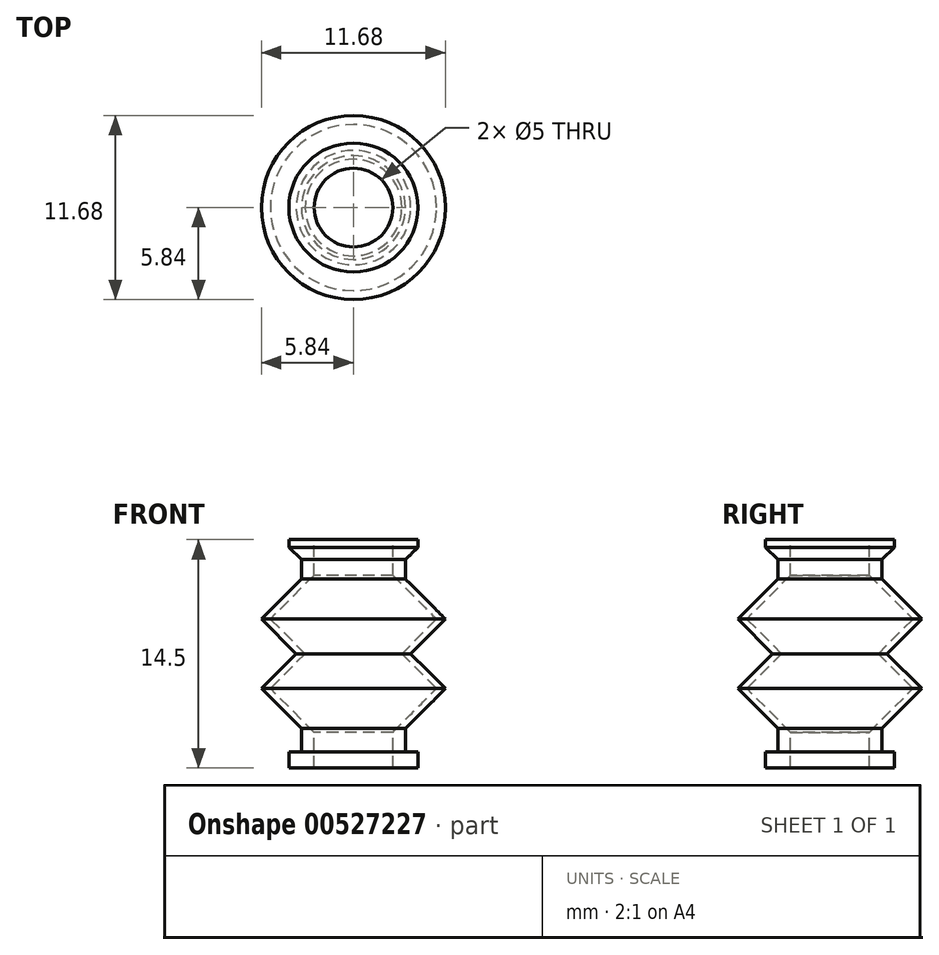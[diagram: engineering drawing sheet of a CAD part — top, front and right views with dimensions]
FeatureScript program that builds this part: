
annotation { "Feature Type Name" : "Feature", "Feature Type Description" : "" }
export const myFeature = defineFeature(function(context is Context, id is Id, definition is map)
    precondition{}
    {
        {
            var Q0;
            Q0=qCreatedBy(makeId("Front.planeOp"),FACE);
            var sketch = newSketch(context, id + "F0", { "sketchPlane" : qUnion([Q0])});
            skLineSegment(sketch, "E0", {"start": v(-2.5, 7.25) * mm, "end": v(-4.1, 7.25) * mm});
            skLineSegment(sketch, "E1", {"start": v(-4.1, 7.25) * mm, "end": v(-4.1, 6.75) * mm});
            skLineSegment(sketch, "E2", {"start": v(0, 8.81) * mm, "end": v(0, -10.41) * mm, "construction": true});
            skLineSegment(sketch, "E3", {"start": v(-2.5, 7.25) * mm, "end": v(-2.5, 4.98) * mm});
            skLineSegment(sketch, "E4.MirrorCS", {"start": v(-2.5, -7.25) * mm, "end": v(-4.1, -7.25) * mm});
            skLineSegment(sketch, "E5.MirrorCS", {"start": v(-4.1, -7.25) * mm, "end": v(-4.1, -6.25) * mm});
            skLineSegment(sketch, "E6.MirrorCS", {"start": v(-2.5, -7.25) * mm, "end": v(-2.5, -4.98) * mm});
            skLineSegment(sketch, "E7.MirrorCS", {"start": v(-3.3, -6.25) * mm, "end": v(-3.3, -4.75) * mm});
            skLineSegment(sketch, "E8", {"start": v(-4.1, -6.25) * mm, "end": v(-3.3, -6.25) * mm});
            skLineSegment(sketch, "E9", {"start": v(-3.3, -4.75) * mm, "end": v(-5.84, -2.2) * mm});
            skLineSegment(sketch, "E10", {"start": v(-5.84, -2.2) * mm, "end": v(-3.64, 0) * mm});
            skLineSegment(sketch, "E11", {"start": v(-2.5, -4.98) * mm, "end": v(-5.28, -2.2) * mm});
            skLineSegment(sketch, "E12", {"start": v(-5.28, -2.2) * mm, "end": v(-3.07, 0) * mm});
            skLineSegment(sketch, "E13", {"start": v(-3.3, 6) * mm, "end": v(-4.1, 6.75) * mm});
            skLineSegment(sketch, "E14.MirrorCS", {"start": v(-3.3, 4.75) * mm, "end": v(-5.84, 2.2) * mm});
            skLineSegment(sketch, "E15.MirrorCS", {"start": v(-5.84, 2.2) * mm, "end": v(-3.64, 0) * mm});
            skLineSegment(sketch, "E16.MirrorCS", {"start": v(-5.28, 2.2) * mm, "end": v(-3.07, 0) * mm});
            skLineSegment(sketch, "E17.MirrorCS", {"start": v(-2.5, 4.98) * mm, "end": v(-5.28, 2.2) * mm});
            skLineSegment(sketch, "E18.MirrorCS", {"start": v(-2.5, 4.98) * mm, "end": v(-2.5, 4.98) * mm});
            skLineSegment(sketch, "E19", {"start": v(-3.3, 6) * mm, "end": v(-3.3, 4.75) * mm});
            skSolve(sketch);
        }
        {
            var Q0;
            Q0=makeQuery(id+"F0.imprint","IMPRINT",FACE,{"disambiguationData":[TD([[makeQuery(id+"F0.imprint","IMPRINT",EDGE,{"derivedFrom":sQuery(id+"F0.wireOp",EDGE,"E0")}),1.0]])]});
            var Q1;
            Q1=sQuery(id+"F0.wireOp",EDGE,"E2");
            revolve(context, id + "F1", {"entities" : qUnion([Q0]), "axis" : qUnion([Q1]), "revolveType" : RevolveType.FULL});
        }
    });
